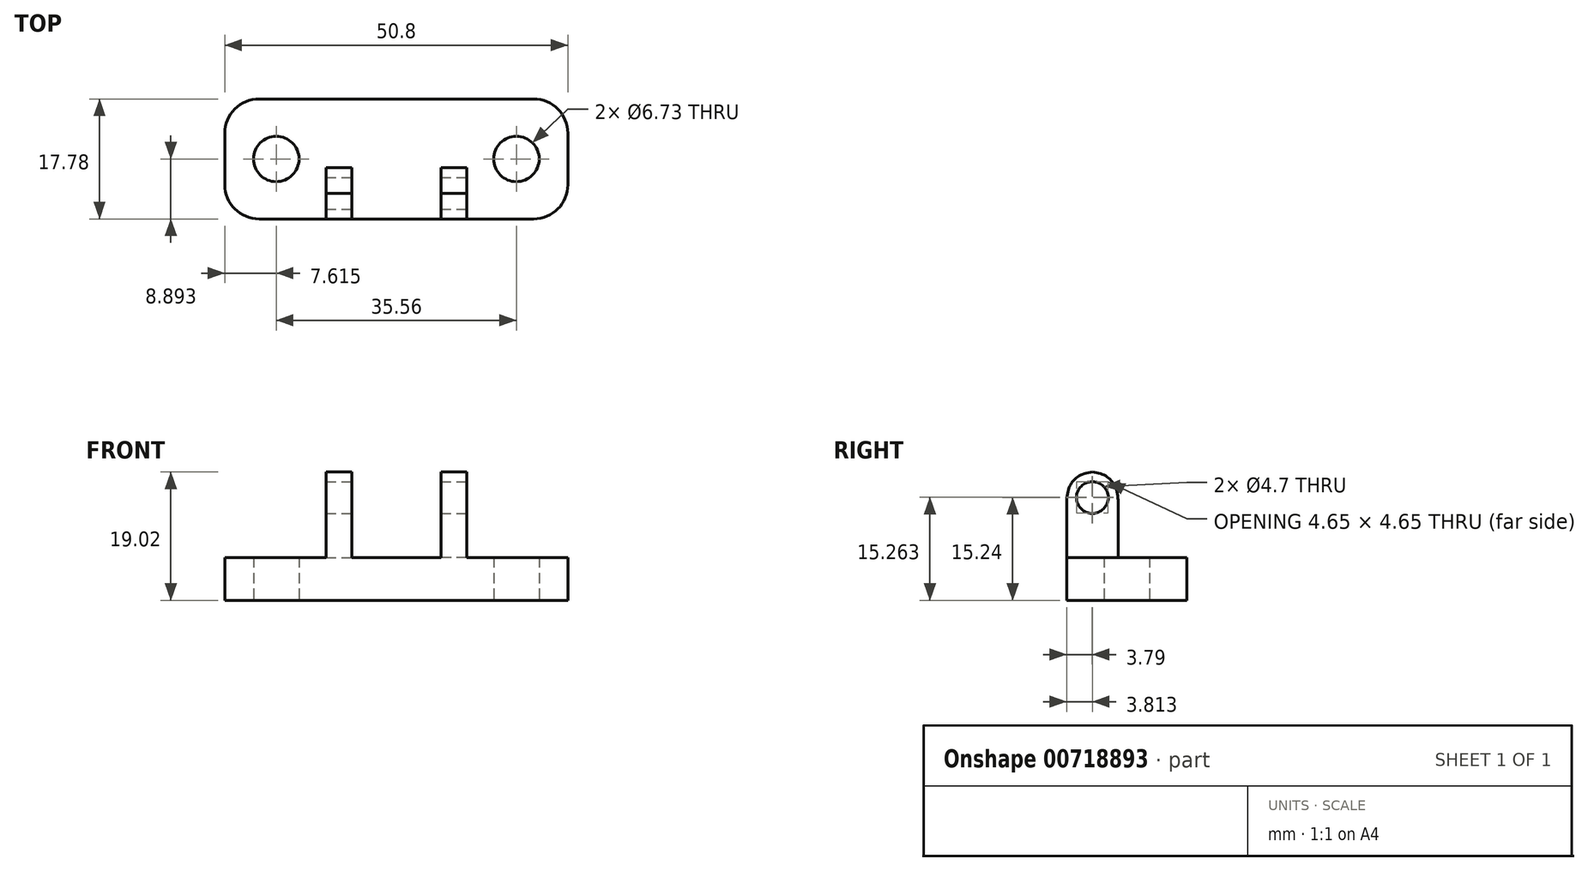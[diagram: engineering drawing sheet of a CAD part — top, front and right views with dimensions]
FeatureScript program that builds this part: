
annotation { "Feature Type Name" : "Feature", "Feature Type Description" : "" }
export const myFeature = defineFeature(function(context is Context, id is Id, definition is map)
    precondition{}
    {
        {
            var Q0;
            Q0=qCreatedBy(makeId("Top.planeOp"),FACE);
            var sketch = newSketch(context, id + "F0", { "sketchPlane" : qUnion([Q0])});
            skLineSegment(sketch, "E0.bottom", {"start": v(-10.8, 6.74) * mm, "end": v(40, 6.74) * mm});
            skLineSegment(sketch, "E0.top", {"start": v(-10.8, -11.04) * mm, "end": v(40, -11.04) * mm});
            skLineSegment(sketch, "E0.left", {"start": v(-10.8, 6.74) * mm, "end": v(-10.8, -11.04) * mm});
            skLineSegment(sketch, "E0.right", {"start": v(40, 6.74) * mm, "end": v(40, -11.04) * mm});
            skCircle(sketch, "E1", {"center": v(-3.17, -2.15) * mm, "radius": 3.37 * mm});
            skCircle(sketch, "E2", {"center": v(32.39, -2.15) * mm, "radius": 3.37 * mm});
            skSolve(sketch);
        }
        {
            var Q0;
            Q0 = qSketchRegion(id + "F0", true);
            extrude(context, id + "F1", {"entities" : qUnion([Q0]), "depth" : 6.35 * mm, "offsetDistance" : 25.4 * mm});
        }
        {
            var Q0;
            Q0=makeQuery(id+"F1.opExtrude","SWEPT_EDGE",EDGE,{"disambiguationData":[OSD([sQuery(id+"F0.wireOp",EDGE,"E0.top"),sQuery(id+"F0.wireOp",EDGE,"E0.right")])]});
            var Q1;
            Q1=makeQuery(id+"F1.opExtrude","SWEPT_EDGE",EDGE,{"disambiguationData":[OSD([sQuery(id+"F0.wireOp",EDGE,"E0.bottom"),sQuery(id+"F0.wireOp",EDGE,"E0.right")])]});
            var Q2;
            Q2=makeQuery(id+"F1.opExtrude","SWEPT_EDGE",EDGE,{"disambiguationData":[OSD([sQuery(id+"F0.wireOp",EDGE,"E0.top"),sQuery(id+"F0.wireOp",EDGE,"E0.left")])]});
            var Q3;
            Q3=makeQuery(id+"F1.opExtrude","SWEPT_EDGE",EDGE,{"disambiguationData":[OSD([sQuery(id+"F0.wireOp",EDGE,"E0.bottom"),sQuery(id+"F0.wireOp",EDGE,"E0.left")])]});
            fillet(context, id + "F2", {"entities" : qUnion([Q0, Q1, Q2, Q3]), "radius" : 5.08 * mm, "tangentPropagation" : true, "allowEdgeOverflow" : false});
        }
        {
            var Q0;
            Q0=makeQuery(id+"F1.opExtrude","CAP_FACE",FACE,{"disambiguationData":[OSD([sQuery(id+"F0.wireOp",EDGE,"E0.bottom"),sQuery(id+"F0.wireOp",EDGE,"E0.top"),sQuery(id+"F0.wireOp",EDGE,"E0.left"),sQuery(id+"F0.wireOp",EDGE,"E0.right"),sQuery(id+"F0.wireOp",EDGE,"E1"),sQuery(id+"F0.wireOp",EDGE,"E2")])],"isStart":false});
            var sketch = newSketch(context, id + "F3", { "sketchPlane" : qUnion([Q0])});
            skLineSegment(sketch, "E3.bottom", {"start": v(4.2, -11.04) * mm, "end": v(8, -11.04) * mm});
            skLineSegment(sketch, "E3.top", {"start": v(4.2, -3.42) * mm, "end": v(8, -3.42) * mm});
            skLineSegment(sketch, "E3.left", {"start": v(4.2, -11.04) * mm, "end": v(4.2, -3.42) * mm});
            skLineSegment(sketch, "E3.right", {"start": v(8, -11.04) * mm, "end": v(8, -3.42) * mm});
            skLineSegment(sketch, "E4", {"start": v(14.6, 6.74) * mm, "end": v(14.6, -11.04) * mm});
            skLineSegment(sketch, "E5.MirrorCS", {"start": v(21.2, -11.04) * mm, "end": v(21.2, -3.42) * mm});
            skLineSegment(sketch, "E6.MirrorCS", {"start": v(25.02, -3.42) * mm, "end": v(21.2, -3.42) * mm});
            skLineSegment(sketch, "E7.MirrorCS", {"start": v(25.02, -11.04) * mm, "end": v(25.02, -3.42) * mm});
            skLineSegment(sketch, "E8.MirrorCS", {"start": v(25.02, -11.04) * mm, "end": v(21.2, -11.04) * mm});
            skSolve(sketch);
        }
        {
            var Q0;
            Q0 = qSketchRegion(id + "F3", true);
            extrude(context, id + "F4", {"entities" : qUnion([Q0]), "operationType" : NewBodyOperationType.ADD, "depth" : 12.7 * mm, "offsetDistance" : 25.4 * mm});
        }
        {
            var Q0;
            Q0=makeQuery(id+"F4.opExtrude","SWEPT_FACE",FACE,{"disambiguationData":[OSD([sQuery(id+"F3.wireOp",EDGE,"E7.MirrorCS")])]});
            var sketch = newSketch(context, id + "F5", { "sketchPlane" : qUnion([Q0])});
            skCircle(sketch, "E9", {"center": v(-7.23, 15.24) * mm, "radius": 2.35 * mm});
            skPoint(sketch, "E9.centerSnap0", {"position": v(-7.23, 19.05) * mm});
            skSolve(sketch);
        }
        {
            var Q0;
            Q0 = qSketchRegion(id + "F5", true);
            extrude(context, id + "F6", {"entities" : qUnion([Q0]), "operationType" : NewBodyOperationType.REMOVE, "oppositeDirection" : true, "depth" : 25.4 * mm, "offsetDistance" : 25.4 * mm});
        }
        {
            var Q0;
            Q0=makeQuery(id+"F4.opExtrude","CAP_EDGE",EDGE,{"disambiguationData":[OSD([sQuery(id+"F3.wireOp",EDGE,"E3.bottom")])],"isStart":false});
            var Q1;
            Q1=makeQuery(id+"F4.opExtrude","CAP_EDGE",EDGE,{"disambiguationData":[OSD([sQuery(id+"F3.wireOp",EDGE,"E3.top")])],"isStart":false});
            var Q2;
            Q2=makeQuery(id+"F4.opExtrude","CAP_EDGE",EDGE,{"disambiguationData":[OSD([sQuery(id+"F3.wireOp",EDGE,"E8.MirrorCS")])],"isStart":false});
            var Q3;
            Q3=makeQuery(id+"F4.opExtrude","CAP_EDGE",EDGE,{"disambiguationData":[OSD([sQuery(id+"F3.wireOp",EDGE,"E6.MirrorCS")])],"isStart":false});
            fillet(context, id + "F7", {"entities" : qUnion([Q0, Q1, Q2, Q3]), "radius" : 4.57 * mm, "tangentPropagation" : true, "rho" : 0.5, "crossSection" : FilletCrossSection.CONIC, "allowEdgeOverflow" : false});
        }
    });
